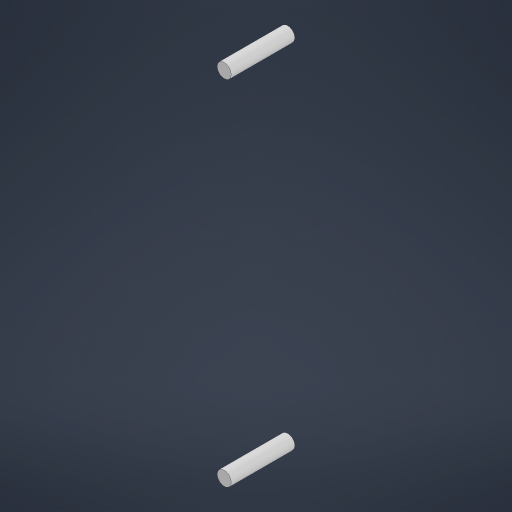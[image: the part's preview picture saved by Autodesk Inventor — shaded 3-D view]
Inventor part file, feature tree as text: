
AUTODESK INVENTOR PART (.ipt)
format: ipt  version: 2024 (Build 280153000, 153)  size: 179,712 bytes
history: native  units: mm
features: other x4, plane x1, extrude x1, sketch x1
ambient origin geometry x8: Origin, YZ Plane, XZ Plane, XY Plane, X Axis, Y Axis, Z Axis, Center Point
bodies: Body1 (feature_tree)
feature tree (7):
  other  "Sólido1"
  plane  "Plano de trabajo1"
  extrude  "Extrusión1"  Depth=18.0mm
  sketch  "Boceto1"  dims[d0=4.0mm d1=4.0mm d2=100.0mm d3=99.2mm d4=7.5mm d5=7.5mm d6=18.0mm d7=0.0mm]
  other  "<userpath>\Downloads\Piezas CMR\Marco_APM_002\Marco_apm_002-4.iam"
  other  "Marco_apm_002-4.iam"
  other  "S_horizontal:1"
